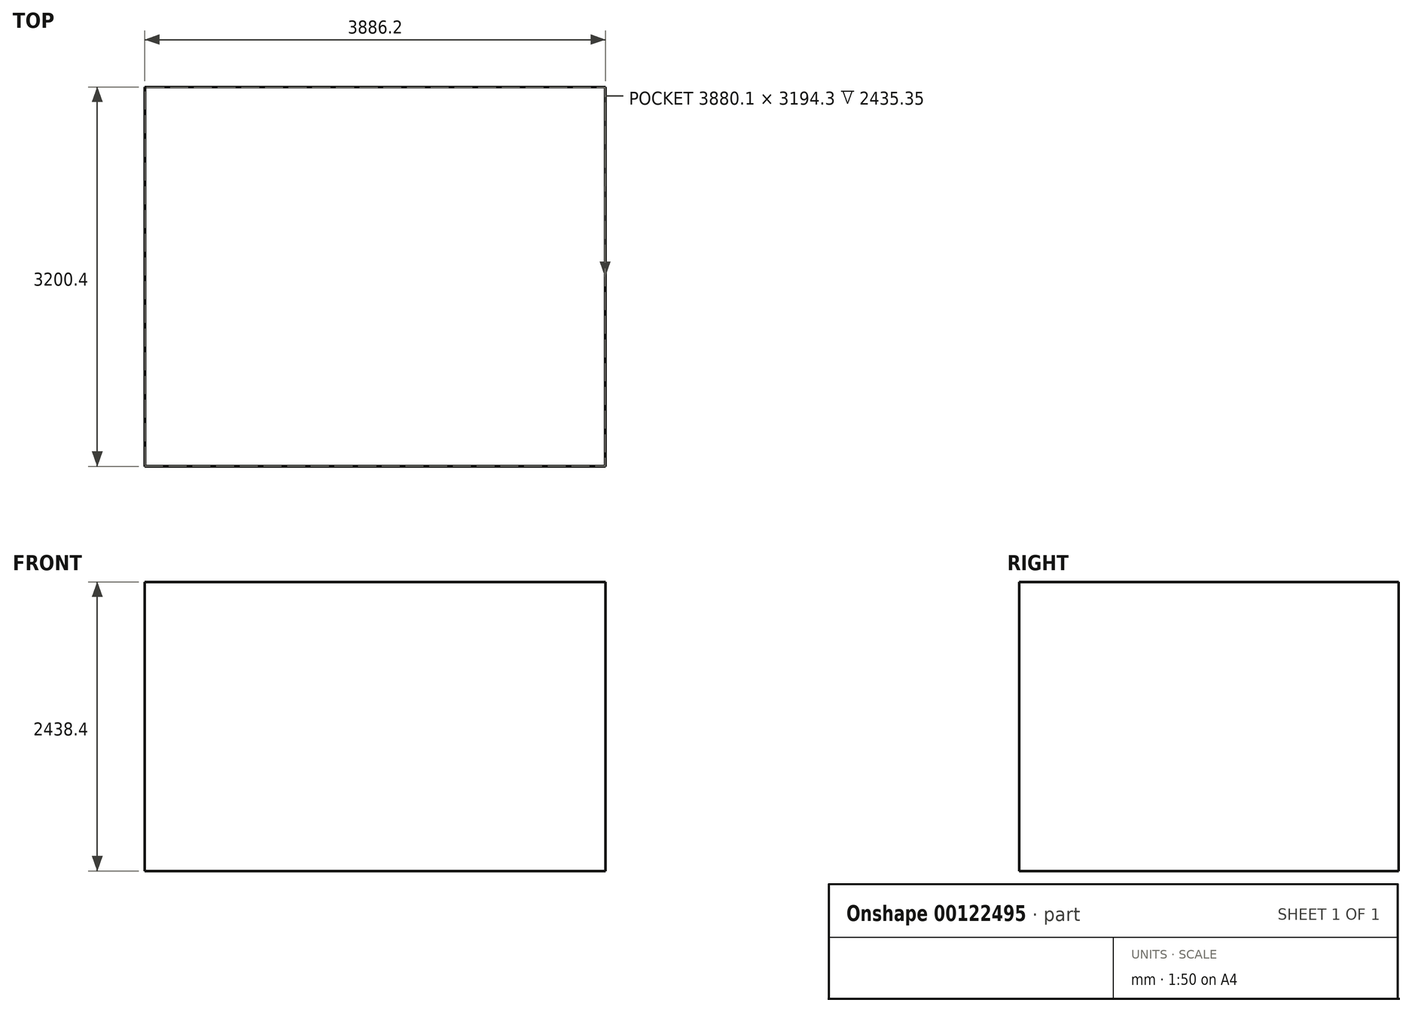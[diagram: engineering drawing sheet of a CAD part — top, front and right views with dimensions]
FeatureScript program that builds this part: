
annotation { "Feature Type Name" : "Feature", "Feature Type Description" : "" }
export const myFeature = defineFeature(function(context is Context, id is Id, definition is map)
    precondition{}
    {
        {
            var Q0;
            Q0=qCreatedBy(makeId("Top.planeOp"),FACE);
            var sketch = newSketch(context, id + "F0", { "sketchPlane" : qUnion([Q0])});
            skLineSegment(sketch, "E0.bottom", {"start": v(-1943.1, -1600.2) * mm, "end": v(1943.1, -1600.2) * mm});
            skLineSegment(sketch, "E0.top", {"start": v(-1943.1, 1600.2) * mm, "end": v(1943.1, 1600.2) * mm});
            skLineSegment(sketch, "E0.left", {"start": v(-1943.1, -1600.2) * mm, "end": v(-1943.1, 1600.2) * mm});
            skLineSegment(sketch, "E0.right", {"start": v(1943.1, -1600.2) * mm, "end": v(1943.1, 1600.2) * mm});
            skPoint(sketch, "E0.middle", {"position": v(0, 0) * mm});
            skSolve(sketch);
        }
        {
            var Q0;
            Q0 = qSketchRegion(id + "F0", true);
            extrude(context, id + "F1", {"entities" : qUnion([Q0]), "depth" : 2438.4 * mm});
        }
        {
            var Q0;
            Q0=makeQuery(id+"F1.opExtrude","CAP_FACE",FACE,{"disambiguationData":[OSD([sQuery(id+"F0.wireOp",EDGE,"E0.bottom"),sQuery(id+"F0.wireOp",EDGE,"E0.top"),sQuery(id+"F0.wireOp",EDGE,"E0.left"),sQuery(id+"F0.wireOp",EDGE,"E0.right")])],"isStart":false});
            var Q1;
            Q1=makeQuery(id+"F1.opExtrude","SWEPT_BODY",BODY,{"disambiguationData":[OSD([sQuery(id+"F0.wireOp",EDGE,"E0.bottom"),sQuery(id+"F0.wireOp",EDGE,"E0.top"),sQuery(id+"F0.wireOp",EDGE,"E0.left"),sQuery(id+"F0.wireOp",EDGE,"E0.right")])]});
            shell(context, id + "F2", {"entities" : qUnion([Q0]), "parts" : qUnion([Q1]), "thickness" : 3.05 * mm});
        }
    });
